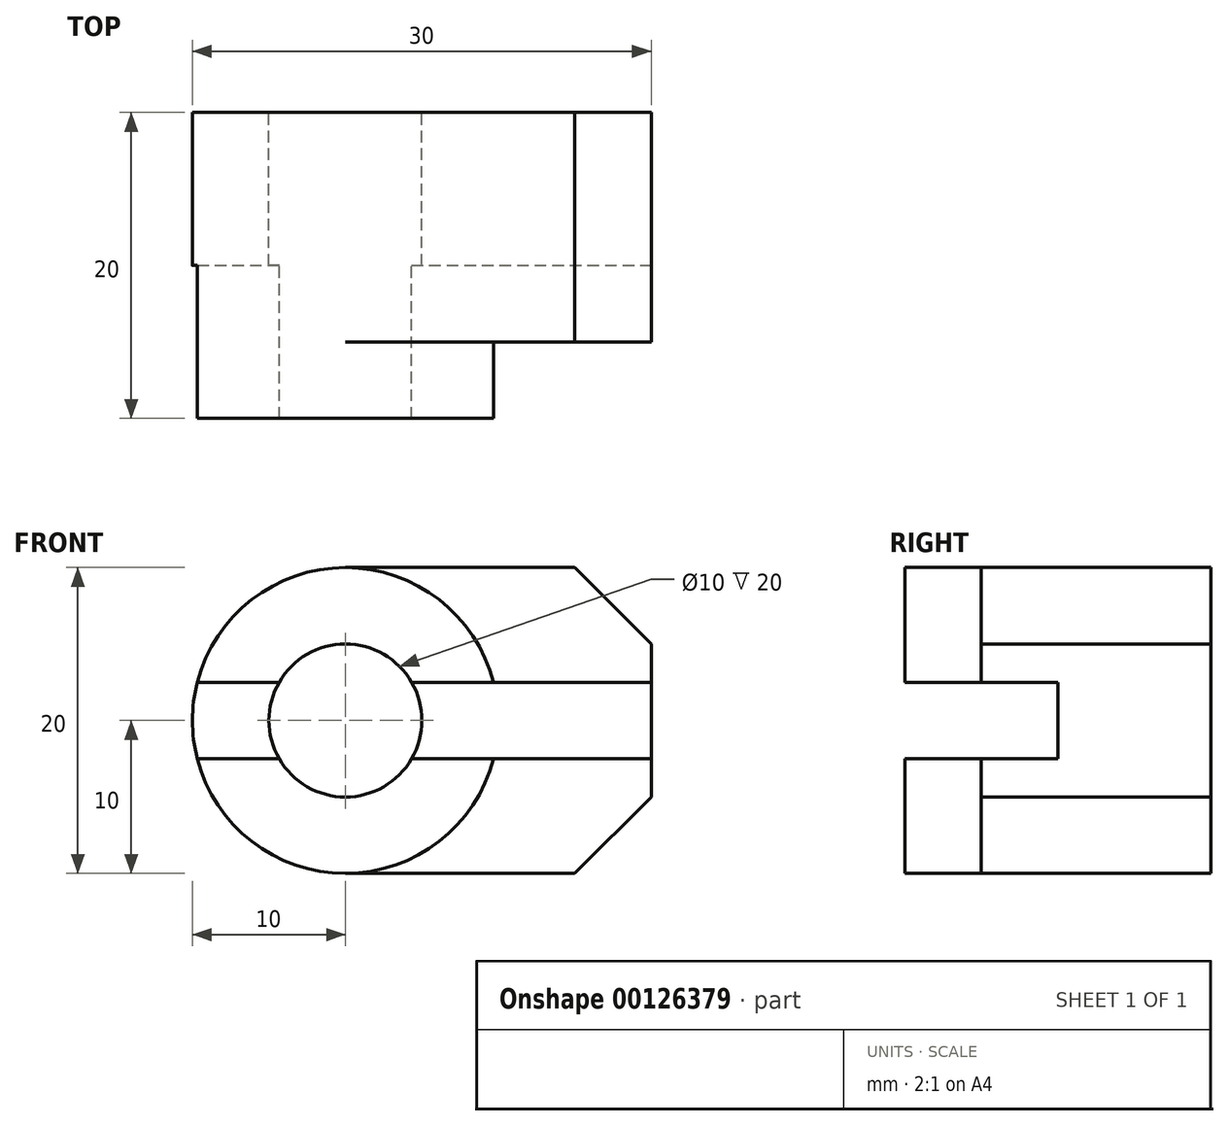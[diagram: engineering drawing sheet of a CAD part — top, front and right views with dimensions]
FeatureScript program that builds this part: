
annotation { "Feature Type Name" : "Feature", "Feature Type Description" : "" }
export const myFeature = defineFeature(function(context is Context, id is Id, definition is map)
    precondition{}
    {
        {
            var Q0;
            Q0=qCreatedBy(makeId("Front.planeOp"),FACE);
            var sketch = newSketch(context, id + "F0", { "sketchPlane" : qUnion([Q0])});
            skCircle(sketch, "E0", {"center": v(0, 0) * mm, "radius": 5 * mm});
            skCircle(sketch, "E1", {"center": v(0, 0) * mm, "radius": 10 * mm});
            skLineSegment(sketch, "E2", {"start": v(0, 10) * mm, "end": v(15, 10) * mm});
            skLineSegment(sketch, "E3", {"start": v(-18.79, 0) * mm, "end": v(35.3, 0) * mm, "construction": true});
            skLineSegment(sketch, "E4", {"start": v(0, -10) * mm, "end": v(15, -10) * mm});
            skLineSegment(sketch, "E5", {"start": v(15, -10) * mm, "end": v(20, -5) * mm});
            skLineSegment(sketch, "E6", {"start": v(20, -5) * mm, "end": v(20, 5) * mm});
            skLineSegment(sketch, "E7", {"start": v(20, 5) * mm, "end": v(15, 10) * mm});
            skLineSegment(sketch, "E8", {"start": v(-9.68, 2.5) * mm, "end": v(-4.33, 2.5) * mm});
            skLineSegment(sketch, "E9", {"start": v(-9.68, -2.5) * mm, "end": v(-4.33, -2.5) * mm});
            skLineSegment(sketch, "E10", {"start": v(4.33, 2.5) * mm, "end": v(20, 2.5) * mm});
            skLineSegment(sketch, "E11", {"start": v(4.33, -2.5) * mm, "end": v(20, -2.5) * mm});
            skSolve(sketch);
        }
        {
            var Q0;
            {var subQ4=sQuery(id+"F0.wireOp",EDGE,"E2");Q0=makeQuery(id+"F0.imprint","IMPRINT",FACE,{"disambiguationData":[TD([[makeQuery(id+"F0.imprint","IMPRINT",EDGE,{"derivedFrom":subQ4}),-1.0]])]});}
            extrude(context, id + "F1", {"entities" : qUnion([Q0]), "depth" : 15 * mm});
        }
        {
            var Q0;
            {var subQ0=sQuery(id+"F0.wireOp",EDGE,"E10");var subQ1=sQuery(id+"F0.wireOp",EDGE,"E1");var subQ2=makeQuery(id+"F0.imprint","INTERSECT",VERTEX,{"derivedFrom":[subQ1,subQ0]});Q0=makeQuery(id+"F0.imprint","IMPRINT",FACE,{"disambiguationData":[TD([[makeQuery(id+"F0.imprint","IMPRINT",EDGE,{"disambiguationData":[TD([[subQ2,1.0]])],"derivedFrom":subQ1}),-1.0]])]});}
            extrude(context, id + "F2", {"entities" : qUnion([Q0]), "operationType" : NewBodyOperationType.ADD, "depth" : 10 * mm});
        }
        {
            var Q0;
            {var subQ4=sQuery(id+"F0.wireOp",EDGE,"E4");Q0=makeQuery(id+"F0.imprint","IMPRINT",FACE,{"disambiguationData":[TD([[makeQuery(id+"F0.imprint","IMPRINT",EDGE,{"derivedFrom":subQ4}),1.0]])]});}
            extrude(context, id + "F3", {"entities" : qUnion([Q0]), "operationType" : NewBodyOperationType.ADD, "depth" : 15 * mm});
        }
        {
            var Q0;
            {var subQ0=sQuery(id+"F0.wireOp",EDGE,"E10");var subQ1=sQuery(id+"F0.wireOp",EDGE,"E0");var subQ2=makeQuery(id+"F0.imprint","INTERSECT",VERTEX,{"derivedFrom":[subQ1,subQ0]});Q0=makeQuery(id+"F0.imprint","IMPRINT",FACE,{"disambiguationData":[TD([[makeQuery(id+"F0.imprint","IMPRINT",EDGE,{"disambiguationData":[TD([[subQ2,1.0]])],"derivedFrom":subQ1}),-1.0]])]});}
            extrude(context, id + "F4", {"entities" : qUnion([Q0]), "operationType" : NewBodyOperationType.ADD, "depth" : 10 * mm});
        }
        {
            var Q0;
            {var subQ2=sQuery(id+"F0.wireOp",EDGE,"E8");Q0=makeQuery(id+"F0.imprint","IMPRINT",FACE,{"disambiguationData":[TD([[makeQuery(id+"F0.imprint","IMPRINT",EDGE,{"derivedFrom":subQ2}),1.0]])]});}
            var Q1;
            {var subQ6=sQuery(id+"F0.wireOp",EDGE,"E9");Q1=makeQuery(id+"F0.imprint","IMPRINT",FACE,{"disambiguationData":[TD([[makeQuery(id+"F0.imprint","IMPRINT",EDGE,{"derivedFrom":subQ6}),-1.0]])]});}
            extrude(context, id + "F5", {"entities" : qUnion([Q0, Q1]), "operationType" : NewBodyOperationType.ADD, "depth" : 20 * mm});
        }
        {
            var Q0;
            {var subQ0=sQuery(id+"F0.wireOp",EDGE,"E8");Q0=makeQuery(id+"F0.imprint","IMPRINT",FACE,{"disambiguationData":[TD([[makeQuery(id+"F0.imprint","IMPRINT",EDGE,{"derivedFrom":subQ0}),-1.0]])]});}
            extrude(context, id + "F6", {"entities" : qUnion([Q0]), "operationType" : NewBodyOperationType.ADD, "depth" : 10 * mm});
        }
    });
